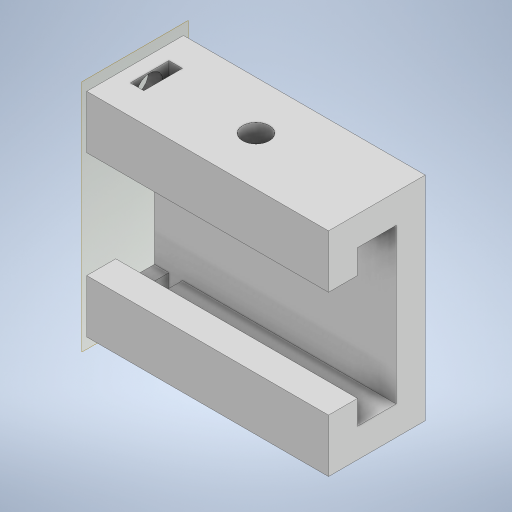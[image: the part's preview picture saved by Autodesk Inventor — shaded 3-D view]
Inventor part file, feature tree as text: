
AUTODESK INVENTOR PART (.ipt)
format: ipt  version: 2023.2 (Build 272271030, 271C)  size: 262,656 bytes
history: native  units: mm
features: extrude x4, sketch x4, plane x2, projected_geometry x1
ambient origin geometry x8: Origin, YZ Plane, XZ Plane, XY Plane, X Axis, Y Axis, Z Axis, Center Point
bodies: Solid1 (feature_tree)
feature tree (11):
  extrude  "Extrusion1"  Depth=32.0mm
  plane  "Work Plane1"
  extrude  "Extrusion2"  Depth=14.0mm
  extrude  "Extrusion3"  Depth=20.0mm
  plane  "Work Plane2"
  extrude  "Extrusion4"  Depth=22.0mm
  sketch  "Sketch1"  dims[d0=22.0mm d1=32.0mm]
  sketch  "Sketch2"  dims[d2=6.0mm d3=14.0mm]
  projected_geometry  "Projected Loop1"
  sketch  "Sketch3"  dims[d4=44.0mm d5=20.0mm]
  sketch  "Sketch4"  dims[d6=50.0mm d7=0.0mm d8=22.0mm d9=5.5mm d10=25.0mm d11=50.0mm d12=0.0mm d13=8.0mm d14=3.0mm d15=2.8mm d16=0.0mm d17=0.0mm d18=-25.0mm d19=5.5mm d20=19.0mm d21=10.0mm d22=0.0mm]
